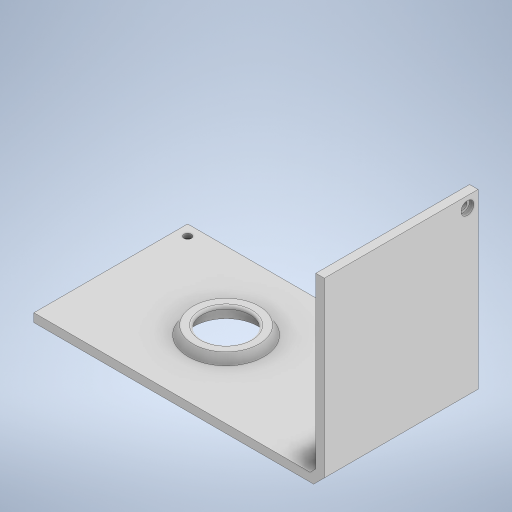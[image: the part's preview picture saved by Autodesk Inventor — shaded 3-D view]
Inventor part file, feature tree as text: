
AUTODESK INVENTOR PART (.ipt)
format: ipt  version: 2023 (Build 270158000, 158)  size: 363,520 bytes
history: native  units: mm
features: sketch x11, extrude x9, projected_geometry x3, other x2, revolve x2, hole x1, fillet x1
ambient origin geometry x8: Origin, YZ Plane, XZ Plane, XY Plane, X Axis, Y Axis, Z Axis, Center Point
bodies: Body1 (feature_tree)
feature tree (29):
  other  "솔리드1"
  extrude  "돌출1"  Depth=140.0mm
  extrude  "돌출2"  Depth=90.0mm
  hole  "구멍1"  [1 undecoded]
  other  "작업 평면1"
  sketch  "스케치5"
  revolve  "회전1"
  revolve  "회전2"
  fillet  "모깎기1"  Radius=5.0mm
  extrude  "돌출3"  Depth=4.0mm
  extrude  "돌출4"  Depth=72.0mm TaperAngle=0.0deg
  extrude  "돌출5"  Depth=53.0mm
  extrude  "돌출6"  Depth=69.0mm
  extrude  "돌출7"  Depth=80.0mm
  extrude  "돌출8"  Depth=65.0mm
  extrude  "돌출9"  Depth=3.0mm
  sketch  "스케치1"
  sketch  "스케치2"
  sketch  "스케치3"
  projected_geometry  "투영된 루프1"
  projected_geometry  "투영된 루프2"
  projected_geometry  "투영된 루프3"
  sketch  "스케치6"
  sketch  "스케치7"
  sketch  "스케치8"
  sketch  "스케치9"
  sketch  "스케치10"
  sketch  "스케치11"
  sketch  "스케치12"
note: 1 required parameter value undecoded (feature->parameter linkage not recoverable at this tier; creation-order binding heuristic only, values carry confidence <= 0.55)
